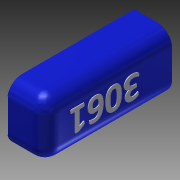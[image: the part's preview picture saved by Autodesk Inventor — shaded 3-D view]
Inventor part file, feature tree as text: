
AUTODESK INVENTOR PART (.ipt)
format: ipt  version: 2013 (Build 170138000, 138)  size: 361,984 bytes
history: native  units: in
note: dims shown in document units (in); Inventor stores cm internally (conversion verified against a paired STEP export)
features: extrude x4, reference x4, sketch x3, fillet x1, projected_geometry x1
ambient origin geometry x8: Origin, YZ Plane, XZ Plane, XY Plane, X Axis, Y Axis, Z Axis, Center Point
bodies: Solid1 (feature_tree)
feature tree (13):
  sketch  "Sketch1"  dims[d0=0.0625in d1=0.0in d3=1.0in]
  extrude  "Extrusion1"  Depth=1.0in
  extrude  "Extrusion2"  Depth=0.0625in
  extrude  "Extrusion3"  Depth=0.0625in TaperAngle=0.0deg
  fillet  "Fillet1"  Radius=1.3125in
  extrude  "Extrusion4"  Depth=6.0in
  reference  "Reference4"
  reference  "Reference5"
  sketch  "Sketch2"  dims[d7=1.0in d9=0.0625in]
  sketch  "Sketch3"  dims[d10=11.25in d11=0.0in d12=0.0625in d13=0.0in d14=1.3125in d15=6.0in d17=1.0in d18=0.0625in d19=0.0in d20=0.0625in d21=0.0625in]
  reference  "Reference6"
  projected_geometry  "Projected Loop1"
  reference  "Reference7"
